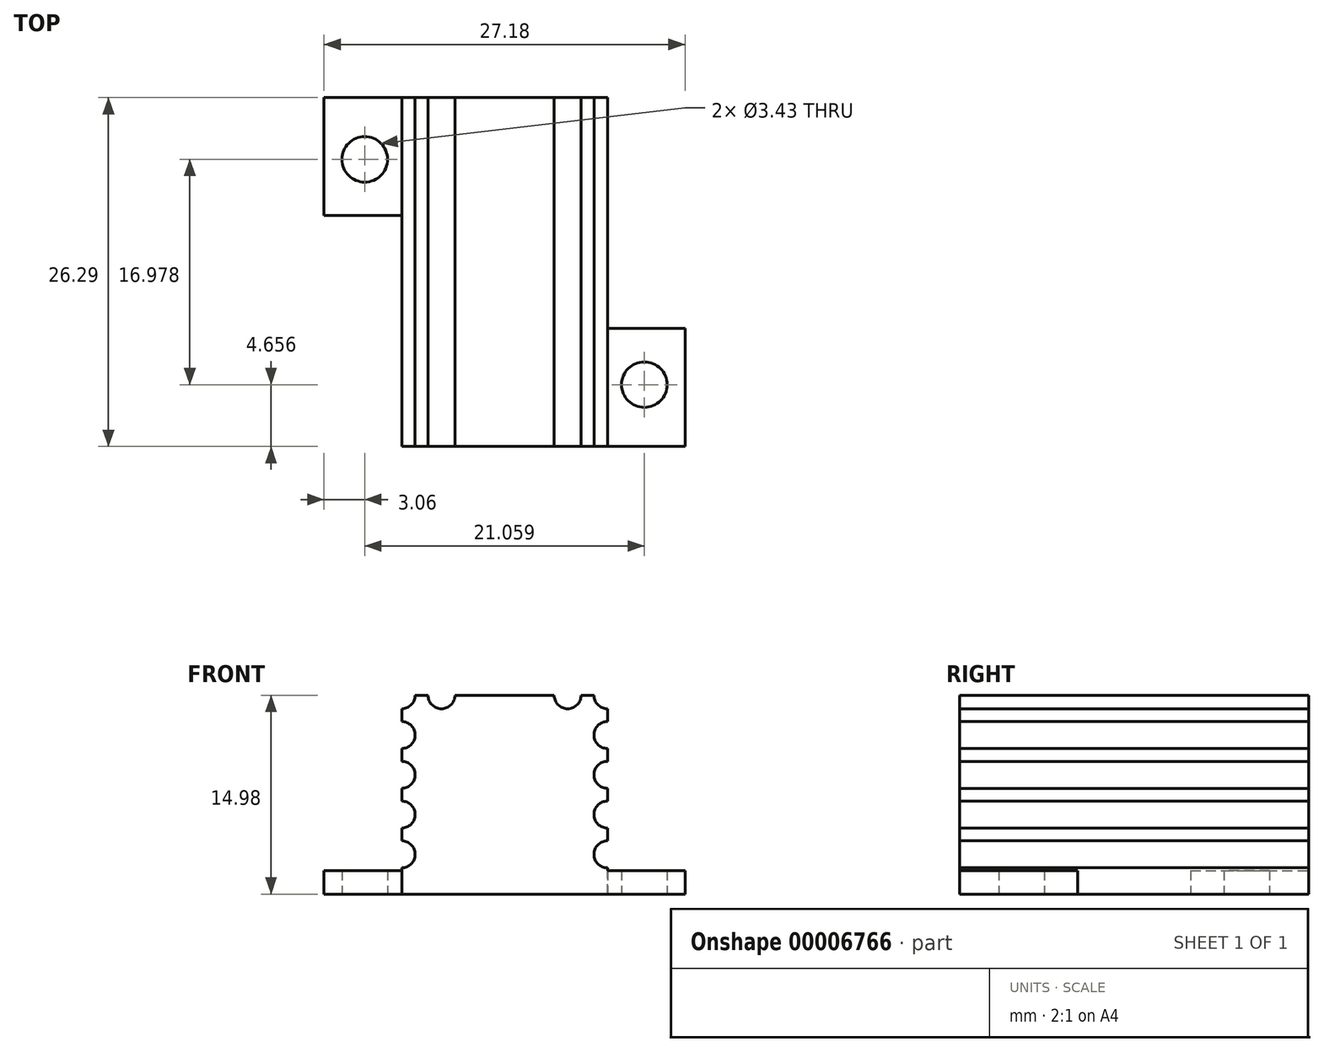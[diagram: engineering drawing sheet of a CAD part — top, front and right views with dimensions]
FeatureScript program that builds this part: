
annotation { "Feature Type Name" : "Feature", "Feature Type Description" : "" }
export const myFeature = defineFeature(function(context is Context, id is Id, definition is map)
    precondition{}
    {
        {
            var Q0;
            Q0=qCreatedBy(makeId("Front.planeOp"),FACE);
            var sketch = newSketch(context, id + "F0", { "sketchPlane" : qUnion([Q0])});
            skLineSegment(sketch, "E0.rect.bottom", {"start": v(7.75, -7.5) * mm, "end": v(-7.75, -7.5) * mm});
            skLineSegment(sketch, "E0.rect.top", {"start": v(7.75, 7.5) * mm, "end": v(4.75, 7.5) * mm});
            skLineSegment(sketch, "E0.rect.left", {"start": v(7.75, -7.5) * mm, "end": v(7.75, -4.5) * mm});
            skLineSegment(sketch, "E0.rect.right", {"start": v(-7.75, -7.5) * mm, "end": v(-7.75, -4.5) * mm});
            skPoint(sketch, "E0.rect.middle", {"position": v(0, 0) * mm});
            skCircle(sketch, "E1", {"center": v(-7.75, 4.5) * mm, "radius": 1.02 * mm});
            skCircle(sketch, "E2", {"center": v(-7.75, 1.5) * mm, "radius": 1.02 * mm});
            skCircle(sketch, "E3", {"center": v(-7.75, -1.5) * mm, "radius": 1.02 * mm});
            skCircle(sketch, "E4", {"center": v(-7.75, -4.5) * mm, "radius": 1.02 * mm});
            skCircle(sketch, "E5", {"center": v(7.75, 4.5) * mm, "radius": 1.02 * mm});
            skCircle(sketch, "E6", {"center": v(7.75, 1.5) * mm, "radius": 1.02 * mm});
            skCircle(sketch, "E7", {"center": v(7.75, -1.5) * mm, "radius": 1.02 * mm});
            skCircle(sketch, "E8", {"center": v(7.75, -4.5) * mm, "radius": 1.02 * mm});
            skCircle(sketch, "E9", {"center": v(-4.75, 7.5) * mm, "radius": 1.02 * mm});
            skCircle(sketch, "E10", {"center": v(4.75, 7.5) * mm, "radius": 1.02 * mm});
            skLineSegment(sketch, "E11", {"start": v(-4.75, 7.5) * mm, "end": v(-7.75, 7.5) * mm});
            skLineSegment(sketch, "E12", {"start": v(4.75, 7.5) * mm, "end": v(-4.75, 7.5) * mm});
            skLineSegment(sketch, "E13", {"start": v(7.75, 4.5) * mm, "end": v(7.75, 7.5) * mm});
            skLineSegment(sketch, "E14", {"start": v(7.75, 1.5) * mm, "end": v(7.75, 4.5) * mm});
            skLineSegment(sketch, "E15", {"start": v(7.75, -1.5) * mm, "end": v(7.75, 1.5) * mm});
            skLineSegment(sketch, "E16", {"start": v(7.75, -4.5) * mm, "end": v(7.75, -1.5) * mm});
            skLineSegment(sketch, "E17", {"start": v(-7.75, -4.5) * mm, "end": v(-7.75, -1.5) * mm});
            skLineSegment(sketch, "E18", {"start": v(-7.75, -1.5) * mm, "end": v(-7.75, 1.5) * mm});
            skLineSegment(sketch, "E19", {"start": v(-7.75, 1.5) * mm, "end": v(-7.75, 4.5) * mm});
            skLineSegment(sketch, "E20", {"start": v(-7.75, 4.5) * mm, "end": v(-7.75, 7.5) * mm});
            skCircle(sketch, "E21", {"center": v(-7.75, 7.5) * mm, "radius": 1.02 * mm});
            skCircle(sketch, "E22", {"center": v(7.75, 7.5) * mm, "radius": 1.02 * mm});
            skSolve(sketch);
        }
        {
            var Q0;
            {var subQ38=sQuery(id+"F0.wireOp",EDGE,"E0.rect.bottom");Q0=makeQuery(id+"F0.imprint","IMPRINT",FACE,{"disambiguationData":[TD([[makeQuery(id+"F0.imprint","IMPRINT",EDGE,{"derivedFrom":subQ38}),-1.0]])]});}
            extrude(context, id + "F1", {"entities" : qUnion([Q0]), "depth" : 26.29 * mm});
        }
        {
            var Q0;
            Q0=makeQuery(id+"F1.opExtrude","SWEPT_FACE",FACE,{"disambiguationData":[OSD([sQuery(id+"F0.wireOp",EDGE,"E0.rect.bottom")])]});
            var sketch = newSketch(context, id + "F2", { "sketchPlane" : qUnion([Q0])});
            skLineSegment(sketch, "E23", {"start": v(7.75, 26.29) * mm, "end": v(13.59, 26.29) * mm});
            skLineSegment(sketch, "E24", {"start": v(13.59, 26.29) * mm, "end": v(13.59, 17.4) * mm});
            skLineSegment(sketch, "E25", {"start": v(13.59, 17.4) * mm, "end": v(7.75, 17.4) * mm});
            skLineSegment(sketch, "E26", {"start": v(-7.75, 0) * mm, "end": v(-13.59, 0) * mm});
            skLineSegment(sketch, "E27", {"start": v(-13.59, 0) * mm, "end": v(-13.59, 8.9) * mm});
            skLineSegment(sketch, "E28", {"start": v(-13.59, 8.9) * mm, "end": v(-7.75, 8.9) * mm});
            skCircle(sketch, "E29", {"center": v(10.53, 21.63) * mm, "radius": 1.71 * mm});
            skCircle(sketch, "E30", {"center": v(-10.53, 4.66) * mm, "radius": 1.71 * mm});
            skLineSegment(sketch, "E31", {"start": v(13.59, 26.29) * mm, "end": v(10.53, 21.63) * mm, "construction": true});
            skLineSegment(sketch, "E32", {"start": v(-7.75, 8.9) * mm, "end": v(-10.53, 4.66) * mm, "construction": true});
            skLineSegment(sketch, "E33", {"start": v(10.53, 21.63) * mm, "end": v(7.75, 17.4) * mm, "construction": true});
            skLineSegment(sketch, "E34", {"start": v(-10.53, 4.66) * mm, "end": v(-13.59, 0) * mm, "construction": true});
            skSolve(sketch);
        }
        {
            var Q0;
            {var subQ3=sQuery(id+"F2.wireOp",EDGE,"E23");Q0=makeQuery(id+"F2.imprint","IMPRINT",FACE,{"disambiguationData":[TD([[makeQuery(id+"F2.imprint","IMPRINT",EDGE,{"derivedFrom":subQ3}),-1.0]])]});}
            var Q1;
            {var subQ3=sQuery(id+"F2.wireOp",EDGE,"E26");Q1=makeQuery(id+"F2.imprint","IMPRINT",FACE,{"disambiguationData":[TD([[makeQuery(id+"F2.imprint","IMPRINT",EDGE,{"derivedFrom":subQ3}),-1.0]])]});}
            extrude(context, id + "F3", {"entities" : qUnion([Q0, Q1]), "operationType" : NewBodyOperationType.ADD, "oppositeDirection" : true, "depth" : 1.78 * mm});
        }
    });
